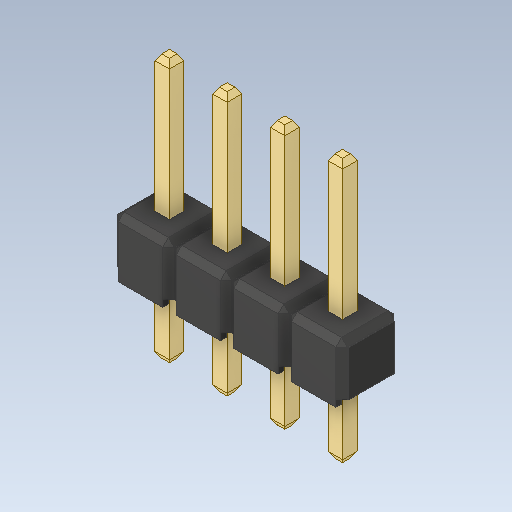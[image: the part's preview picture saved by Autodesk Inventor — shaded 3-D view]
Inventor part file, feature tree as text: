
AUTODESK INVENTOR PART (.ipt)
format: ipt  version: 2020 (Build 240168000, 168)  size: 212,992 bytes
history: native  units: in
note: dims shown in document units (in); Inventor stores cm internally (conversion verified against a paired STEP export)
features: other x7, chamfer x1
ambient origin geometry x8: Origin, YZ Plane, XZ Plane, XY Plane, X Axis, Y Axis, Z Axis, Center Point
bodies: Solid1 (feature_tree), Solid2 (feature_tree), Solid3 (feature_tree), Solid4 (feature_tree), Solid5 (feature_tree), Solid6 (feature_tree), Solid7 (feature_tree), Solid8 (feature_tree)
feature tree (8):
  chamfer  "Chamfer2"  [1 undecoded]
  other  "Boss-Extrude3"
  other  "LPattern1[1]"
  other  "LPattern1[2]"
  other  "LPattern1[3]"
  other  "LPattern1[4]"
  other  "LPattern1[5]"
  other  "LPattern1[6]"
note: 1 required parameter value undecoded (feature->parameter linkage not recoverable at this tier; creation-order binding heuristic only, values carry confidence <= 0.55)
